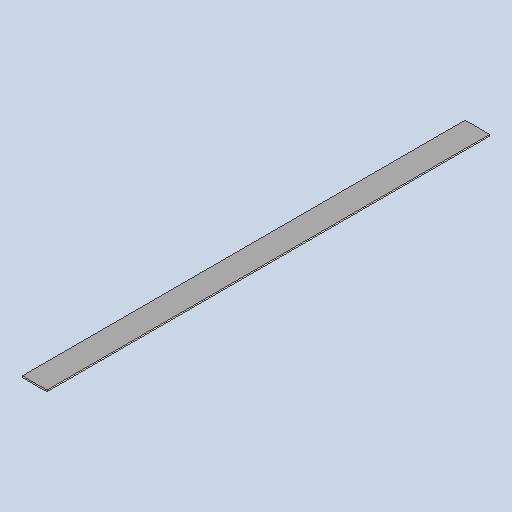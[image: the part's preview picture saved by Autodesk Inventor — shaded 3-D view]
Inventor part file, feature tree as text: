
AUTODESK INVENTOR PART (.ipt)
format: ipt  version: 2025 (Build 290162010, 162A)  size: 278,016 bytes
history: native  units: mm
features: other x3, sheet_metal_op x1, sketch x1
ambient origin geometry x8: Origin, YZ Plane, XZ Plane, XY Plane, X Axis, Y Axis, Z Axis, Center Point
bodies: Body1 (feature_tree)
feature tree (5):
  other  "BSH 503 inner cross"
  sheet_metal_op  "Face2"
  sketch  "Sketch1"  dims[d11=1100.0mm d12=900.0mm d13=25.0mm d14=25.0mm d15=3.0mm]
  other  "Plate2"
  other  "Definition1"
